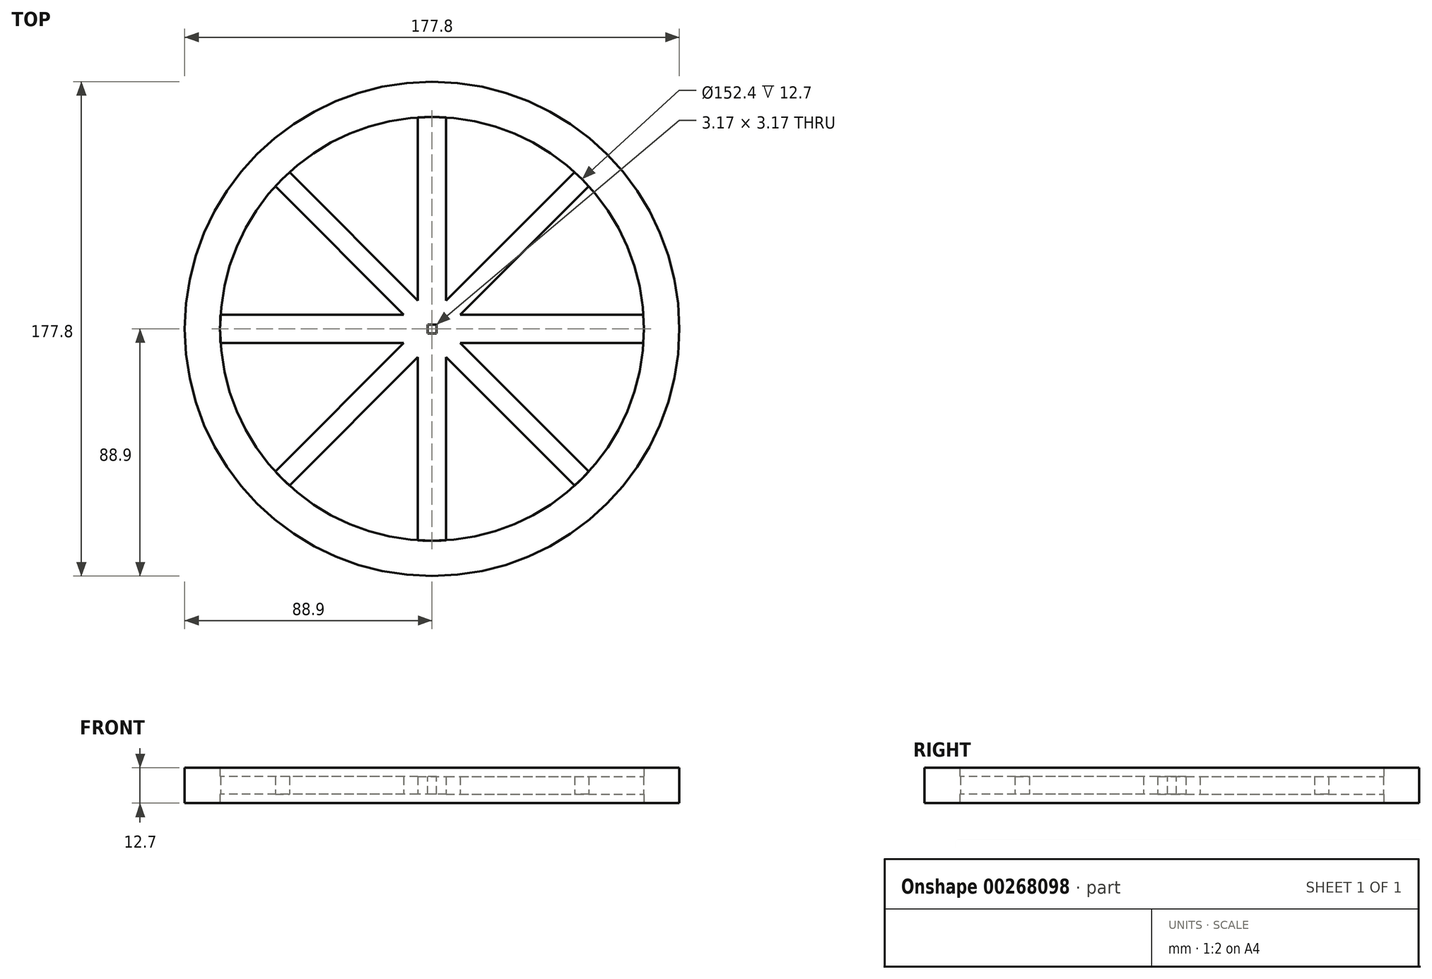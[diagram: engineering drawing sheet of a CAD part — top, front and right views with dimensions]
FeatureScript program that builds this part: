
annotation { "Feature Type Name" : "Feature", "Feature Type Description" : "" }
export const myFeature = defineFeature(function(context is Context, id is Id, definition is map)
    precondition{}
    {
        {
            var Q0;
            Q0=qCreatedBy(makeId("Top.planeOp"),FACE);
            var sketch = newSketch(context, id + "F0", { "sketchPlane" : qUnion([Q0])});
            skCircle(sketch, "E0", {"center": v(0, 0) * mm, "radius": 88.9 * mm});
            skCircle(sketch, "E1", {"center": v(0, 0) * mm, "radius": 76.2 * mm});
            skLineSegment(sketch, "E2", {"start": v(10.16, 5.08) * mm, "end": v(76.03, 5.08) * mm});
            skLineSegment(sketch, "E3.MirrorCS", {"start": v(10.16, -5.08) * mm, "end": v(76.03, -5.08) * mm});
            skLineSegment(sketch, "E4", {"start": v(5.08, -10.16) * mm, "end": v(5.08, -76.03) * mm});
            skLineSegment(sketch, "E5.MirrorCS", {"start": v(-5.08, -10.16) * mm, "end": v(-5.08, -76.03) * mm});
            skLineSegment(sketch, "E6.MirrorCS", {"start": v(5.08, 10.16) * mm, "end": v(5.08, 76.03) * mm});
            skLineSegment(sketch, "E7", {"start": v(-10.16, -5.08) * mm, "end": v(-56.36, -51.28) * mm});
            skLineSegment(sketch, "E8", {"start": v(-5.08, -10.16) * mm, "end": v(-51.28, -56.36) * mm});
            skLineSegment(sketch, "E9", {"start": v(-10.16, 5.08) * mm, "end": v(-56.36, 51.28) * mm});
            skLineSegment(sketch, "E10", {"start": v(-5.08, 10.16) * mm, "end": v(-51.28, 56.36) * mm});
            skLineSegment(sketch, "E11", {"start": v(5.08, -10.16) * mm, "end": v(51.28, -56.36) * mm});
            skLineSegment(sketch, "E12", {"start": v(10.16, -5.08) * mm, "end": v(56.36, -51.28) * mm});
            skLineSegment(sketch, "E13", {"start": v(5.08, 10.16) * mm, "end": v(51.28, 56.36) * mm});
            skLineSegment(sketch, "E14", {"start": v(10.16, 5.08) * mm, "end": v(56.36, 51.28) * mm});
            skPoint(sketch, "E15.orphan", {"position": v(-93.75, 93.75) * mm});
            skPoint(sketch, "E16.orphan", {"position": v(125.72, 125.72) * mm});
            skPoint(sketch, "E17.orphan", {"position": v(-5.08, 109.43) * mm});
            skPoint(sketch, "E18.orphan", {"position": v(0, 99.77) * mm});
            skPoint(sketch, "E19.orphan", {"position": v(5.08, 109.43) * mm});
            skPoint(sketch, "E20.orphan", {"position": v(119.71, 5.08) * mm});
            skPoint(sketch, "E21.orphan", {"position": v(119.71, -5.08) * mm});
            skPoint(sketch, "E22.trimOffspring.end.orphan", {"position": v(-119.71, -5.08) * mm});
            skPoint(sketch, "E23.start.orphan", {"position": v(-137.91, 0) * mm});
            skPoint(sketch, "E24.trimOffspring.end.orphan", {"position": v(-119.71, 5.08) * mm});
            skPoint(sketch, "E25.orphan", {"position": v(-125.72, -125.72) * mm});
            skPoint(sketch, "E26.trimOffspring.end.orphan", {"position": v(93.75, -93.75) * mm});
            skPoint(sketch, "E27.orphan", {"position": v(-5.08, -109.43) * mm});
            skPoint(sketch, "E28.orphan", {"position": v(5.08, -109.43) * mm});
            skLineSegment(sketch, "E29.trimOffspring", {"start": v(-5.08, 10.16) * mm, "end": v(-5.08, 76.03) * mm});
            skLineSegment(sketch, "E30.trimOffspring", {"start": v(-10.16, 5.08) * mm, "end": v(-76.03, 5.08) * mm});
            skPoint(sketch, "E31.MirrorCS.start.orphan", {"position": v(0, 5.08) * mm});
            skPoint(sketch, "E32.orphan", {"position": v(-5.08, 0) * mm});
            skLineSegment(sketch, "E33.trimOffspring", {"start": v(-10.16, -5.08) * mm, "end": v(-76.03, -5.08) * mm});
            skPoint(sketch, "E34.MirrorCS.start.orphan", {"position": v(0, -5.08) * mm});
            skSolve(sketch);
        }
        {
            var Q0;
            Q0=makeQuery(id+"F0.imprint","IMPRINT",FACE,{"disambiguationData":[TD([[makeQuery(id+"F0.imprint","IMPRINT",EDGE,{"derivedFrom":sQuery(id+"F0.wireOp",EDGE,"E0")}),1.0]])]});
            extrude(context, id + "F1", {"entities" : qUnion([Q0]), "depth" : 6.35 * mm, "hasSecondDirection" : true, "secondDirectionOppositeDirection" : true, "secondDirectionDepth" : 6.35 * mm});
        }
        {
            var Q0;
            {var subQ14=sQuery(id+"F0.wireOp",EDGE,"E2");Q0=makeQuery(id+"F0.imprint","IMPRINT",FACE,{"disambiguationData":[TD([[makeQuery(id+"F0.imprint","IMPRINT",EDGE,{"derivedFrom":subQ14}),-1.0]])]});}
            extrude(context, id + "F2", {"entities" : qUnion([Q0]), "operationType" : NewBodyOperationType.ADD, "depth" : 3.17 * mm, "hasSecondDirection" : true, "secondDirectionOppositeDirection" : true, "secondDirectionDepth" : 3.17 * mm});
        }
        {
            var Q0;
            {var subQ0=sQuery(id+"F0.wireOp",EDGE,"E9");Q0=makeQuery(id+"F0.imprint","IMPRINT",FACE,{"disambiguationData":[TD([[makeQuery(id+"F0.imprint","IMPRINT",EDGE,{"derivedFrom":subQ0}),1.0]])]});}
            var sketch = newSketch(context, id + "F3", { "sketchPlane" : qUnion([Q0])});
            skLineSegment(sketch, "E35.bottom", {"start": v(1.59, 1.59) * mm, "end": v(-1.59, 1.59) * mm});
            skLineSegment(sketch, "E35.top", {"start": v(1.59, -1.59) * mm, "end": v(-1.59, -1.59) * mm});
            skLineSegment(sketch, "E35.left", {"start": v(1.59, 1.59) * mm, "end": v(1.59, -1.59) * mm});
            skLineSegment(sketch, "E35.right", {"start": v(-1.59, 1.59) * mm, "end": v(-1.59, -1.59) * mm});
            skPoint(sketch, "E35.middle", {"position": v(0, 0) * mm});
            skSolve(sketch);
        }
        {
            var Q0;
            Q0 = qSketchRegion(id + "F3", true);
            extrude(context, id + "F4", {"entities" : qUnion([Q0]), "operationType" : NewBodyOperationType.REMOVE, "oppositeDirection" : true, "depth" : 127 * mm, "hasSecondDirection" : true, "secondDirectionOppositeDirection" : false, "secondDirectionDepth" : 25.4 * mm});
        }
    });
